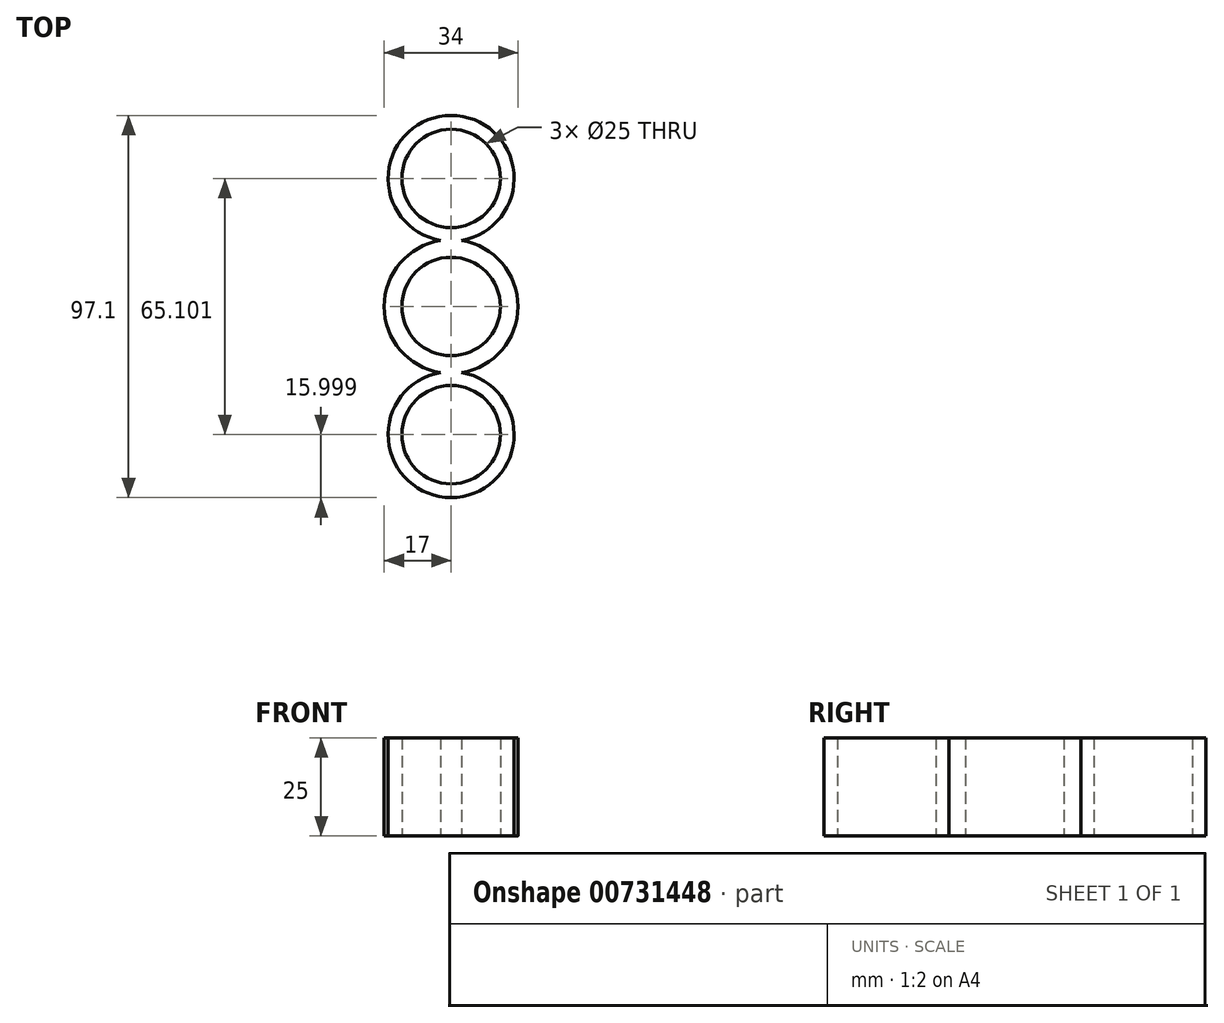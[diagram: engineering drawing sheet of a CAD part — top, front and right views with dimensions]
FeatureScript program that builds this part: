
annotation { "Feature Type Name" : "Feature", "Feature Type Description" : "" }
export const myFeature = defineFeature(function(context is Context, id is Id, definition is map)
    precondition{}
    {
        {
            var Q0;
            Q0=qCreatedBy(makeId("Top.planeOp"),FACE);
            var sketch = newSketch(context, id + "F0", { "sketchPlane" : qUnion([Q0])});
            skCircle(sketch, "E0", {"center": v(0, 0) * mm, "radius": 12.5 * mm});
            skCircle(sketch, "E1", {"center": v(0, -32.55) * mm, "radius": 12.5 * mm});
            skArc(sketch, "E2", {"start": v(-2.71, -16.78) * mm, "mid": v(0, -48.55) * mm, "end": v(2.71, -16.78) * mm});
            skArc(sketch, "E3", {"start": v(2.71, -16.78) * mm, "mid": v(17, 0) * mm, "end": v(2.71, 16.78) * mm});
            skCircle(sketch, "E4.MirrorC", {"center": v(0, 32.55) * mm, "radius": 12.5 * mm});
            skArc(sketch, "E5.MirrorCS", {"start": v(-2.71, 16.78) * mm, "mid": v(0, 48.55) * mm, "end": v(2.71, 16.78) * mm});
            skArc(sketch, "E6.MirrorCS", {"start": v(2.71, 16.78) * mm, "mid": v(17, 0) * mm, "end": v(2.71, -16.78) * mm});
            skArc(sketch, "E7.trimOffspring", {"start": v(-2.71, 16.78) * mm, "mid": v(-17, 0) * mm, "end": v(-2.71, -16.78) * mm});
            skArc(sketch, "E8.trimOffspring", {"start": v(-2.71, -16.78) * mm, "mid": v(-17, 0) * mm, "end": v(-2.71, 16.78) * mm});
            skSolve(sketch);
        }
        {
            var Q0;
            Q0 = qSketchRegion(id + "F0", true);
            extrude(context, id + "F1", {"entities" : qUnion([Q0]), "depth" : 25 * mm, "offsetDistance" : 25 * mm});
        }
    });
